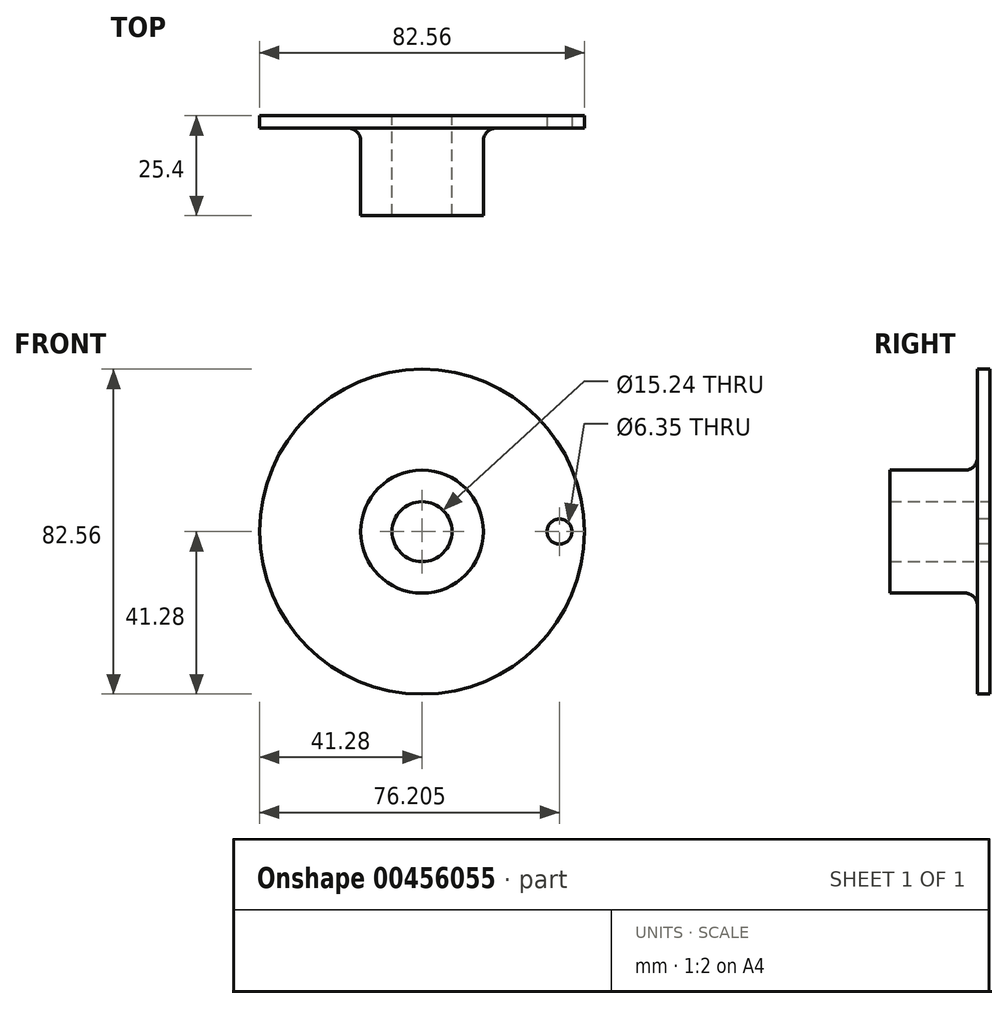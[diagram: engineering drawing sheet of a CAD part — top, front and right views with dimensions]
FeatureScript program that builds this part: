
annotation { "Feature Type Name" : "Feature", "Feature Type Description" : "" }
export const myFeature = defineFeature(function(context is Context, id is Id, definition is map)
    precondition{}
    {
        {
            var Q0;
            Q0=qCreatedBy(makeId("Front.planeOp"),FACE);
            var sketch = newSketch(context, id + "F0", { "sketchPlane" : qUnion([Q0])});
            skCircle(sketch, "E0", {"center": v(0, 0) * mm, "radius": 41.28 * mm});
            skSolve(sketch);
        }
        {
            var Q0;
            Q0 = qSketchRegion(id + "F0", true);
            extrude(context, id + "F1", {"entities" : qUnion([Q0]), "depth" : 3.17 * mm});
        }
        {
            var Q0;
            Q0=qCreatedBy(makeId("Front.planeOp"),FACE);
            var sketch = newSketch(context, id + "F2", { "sketchPlane" : qUnion([Q0])});
            skCircle(sketch, "E1", {"center": v(0, 0) * mm, "radius": 15.6 * mm});
            skSolve(sketch);
        }
        {
            var Q0;
            Q0=makeQuery(id+"F2.imprint","IMPRINT",FACE,{"disambiguationData":[TD([[makeQuery(id+"F2.imprint","IMPRINT",EDGE,{"derivedFrom":sQuery(id+"F2.wireOp",EDGE,"E1")}),1.0]])]});
            extrude(context, id + "F3", {"entities" : qUnion([Q0]), "operationType" : NewBodyOperationType.ADD, "depth" : 25.4 * mm});
        }
        {
            var Q0;
            Q0=qCreatedBy(makeId("Front.planeOp"),FACE);
            var sketch = newSketch(context, id + "F4", { "sketchPlane" : qUnion([Q0])});
            skCircle(sketch, "E2", {"center": v(0, 0) * mm, "radius": 7.62 * mm});
            skSolve(sketch);
        }
        {
            var Q0;
            Q0 = qSketchRegion(id + "F4", true);
            extrude(context, id + "F5", {"entities" : qUnion([Q0]), "operationType" : NewBodyOperationType.REMOVE, "depth" : 25.4 * mm});
        }
        {
            var Q0;
            Q0=makeQuery(id+"F3.boolean.opBoolean","INTERSECT",EDGE,{"derivedFrom":[makeQuery(id+"F1.opExtrude","CAP_FACE",FACE,{"disambiguationData":[OSD([sQuery(id+"F0.wireOp",EDGE,"E0")])],"isStart":false}),makeQuery(id+"F3.opExtrude","SWEPT_FACE",FACE,{"disambiguationData":[OSD([sQuery(id+"F2.wireOp",EDGE,"E1")])]})]});
            fillet(context, id + "F6", {"entities" : qUnion([Q0]), "radius" : 3.17 * mm, "tangentPropagation" : true, "allowEdgeOverflow" : false});
        }
        {
            var Q0;
            Q0=makeQuery(id+"F1.opExtrude","CAP_FACE",FACE,{"disambiguationData":[OSD([sQuery(id+"F0.wireOp",EDGE,"E0")])],"isStart":false});
            var sketch = newSketch(context, id + "F7", { "sketchPlane" : qUnion([Q0])});
            skCircle(sketch, "E3", {"center": v(0, 0) * mm, "radius": 34.93 * mm, "construction": true});
            skSolve(sketch);
        }
        {
            var Q0;
            {var subQ0=sQuery(id+"F0.wireOp",EDGE,"E0");Q0=makeQuery(id+"F7.imprint","IMPRINT",FACE,{"disambiguationData":[TD([[makeQuery(id+"F7.imprint","IMPRINT",EDGE,{"derivedFrom":makeQuery(id+"F1.opExtrude","CAP_EDGE",EDGE,{"disambiguationData":[OSD([subQ0])],"isStart":false})}),1.0]])]});}
            var sketch = newSketch(context, id + "F8", { "sketchPlane" : qUnion([Q0])});
            skCircle(sketch, "E4", {"center": v(34.93, 0) * mm, "radius": 3.18 * mm});
            skSolve(sketch);
        }
        {
            var Q0;
            Q0=makeQuery(id+"F8.imprint","IMPRINT",FACE,{"disambiguationData":[TD([[makeQuery(id+"F8.imprint","IMPRINT",EDGE,{"derivedFrom":sQuery(id+"F8.wireOp",EDGE,"E4")}),1.0]])]});
            var Q1;
            Q1=sQuery(id+"F8.wireOp",EDGE,"E4");
            extrude(context, id + "F9", {"entities" : qUnion([Q0]), "operationType" : NewBodyOperationType.REMOVE, "surfaceEntities" : qUnion([Q1]), "oppositeDirection" : true, "depth" : 25.4 * mm});
        }
    });
